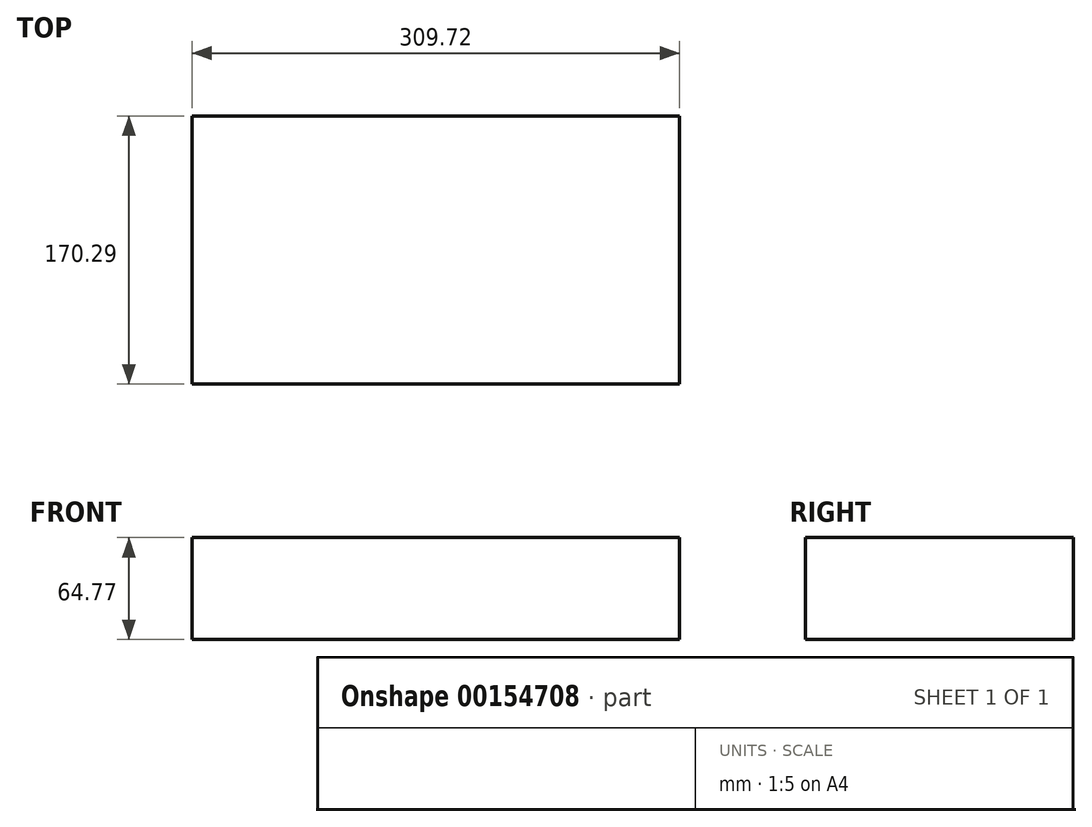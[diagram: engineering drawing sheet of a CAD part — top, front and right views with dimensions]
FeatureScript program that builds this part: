
annotation { "Feature Type Name" : "Feature", "Feature Type Description" : "" }
export const myFeature = defineFeature(function(context is Context, id is Id, definition is map)
    precondition{}
    {
        {
            var Q0;
            Q0=qCreatedBy(makeId("Top.planeOp"),FACE);
            var sketch = newSketch(context, id + "F0", { "sketchPlane" : qUnion([Q0])});
            skLineSegment(sketch, "E0.bottom", {"start": v(-155.18, -85.33) * mm, "end": v(154.54, -85.33) * mm});
            skLineSegment(sketch, "E0.top", {"start": v(-155.18, 84.96) * mm, "end": v(154.54, 84.96) * mm});
            skLineSegment(sketch, "E0.left", {"start": v(-155.18, -85.33) * mm, "end": v(-155.18, 84.96) * mm});
            skLineSegment(sketch, "E0.right", {"start": v(154.54, -85.33) * mm, "end": v(154.54, 84.96) * mm});
            skSolve(sketch);
        }
        {
            var Q0;
            Q0 = qSketchRegion(id + "F0", true);
            extrude(context, id + "F1", {"entities" : qUnion([Q0]), "depth" : 64.77 * mm});
        }
    });
